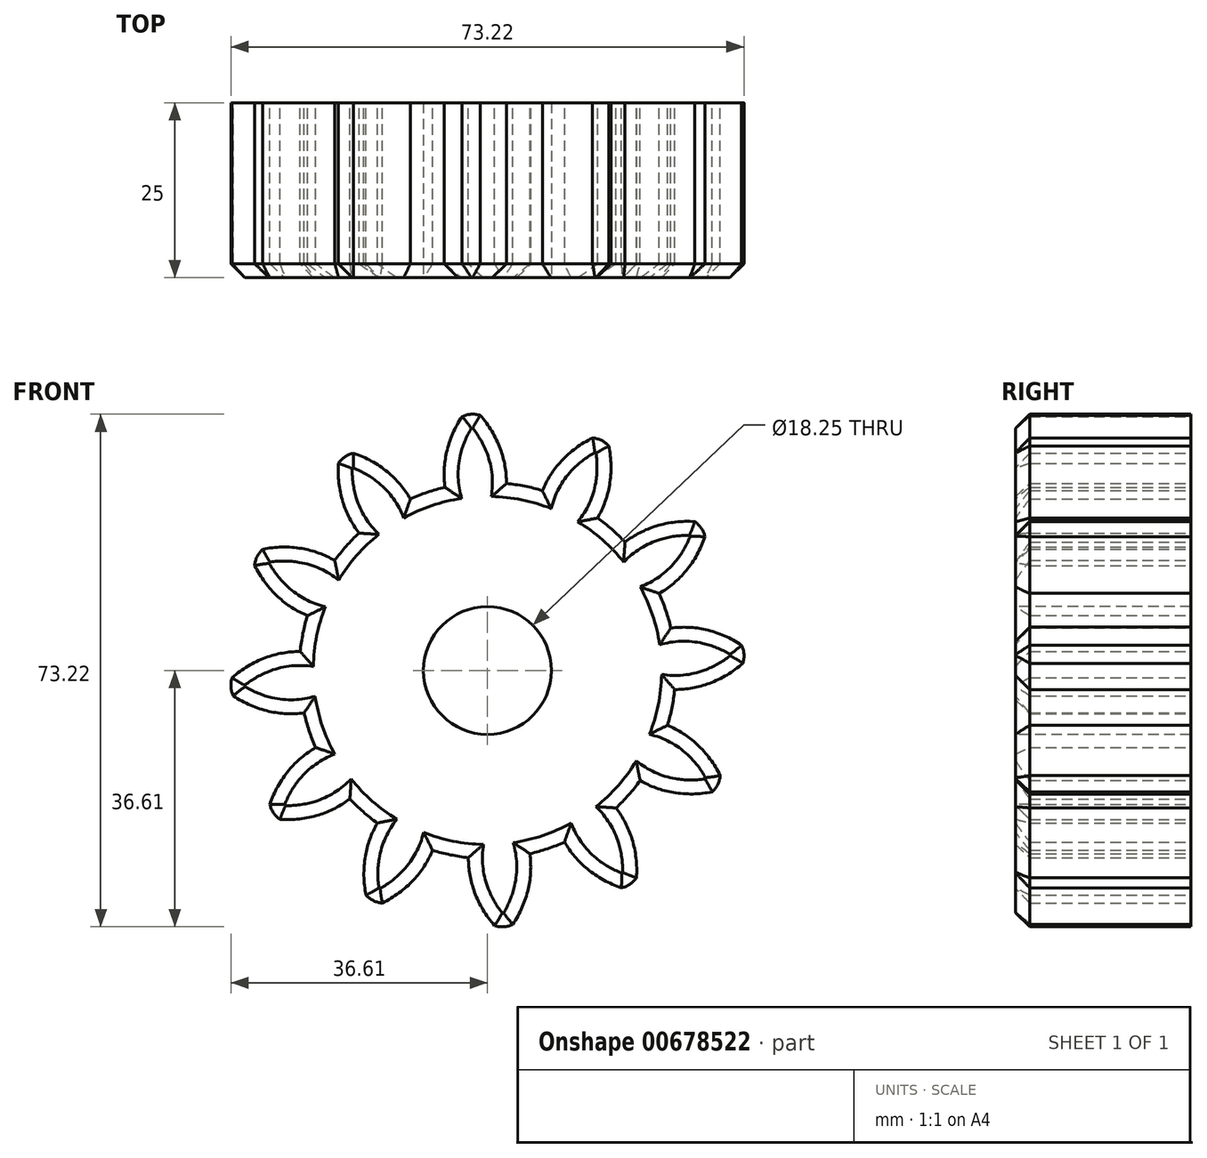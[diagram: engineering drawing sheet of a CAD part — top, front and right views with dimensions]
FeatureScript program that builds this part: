
annotation { "Feature Type Name" : "Feature", "Feature Type Description" : "" }
export const myFeature = defineFeature(function(context is Context, id is Id, definition is map)
    precondition{}
    {
        {
            var Q0;
            Q0=qCreatedBy(makeId("Front.planeOp"),FACE);
            var sketch = newSketch(context, id + "F0", { "sketchPlane" : qUnion([Q0])});
            skCircle(sketch, "E0", {"center": v(0, 0) * mm, "radius": 26.86 * mm});
            skCircle(sketch, "E1", {"center": v(0, 0) * mm, "radius": 29.34 * mm, "construction": true});
            skCircle(sketch, "E2", {"center": v(0, 0) * mm, "radius": 31.75 * mm, "construction": true});
            skLineSegment(sketch, "E3", {"start": v(0, 0) * mm, "end": v(0, 50.88) * mm, "construction": true});
            skLineSegment(sketch, "E4", {"start": v(0, 0) * mm, "end": v(-3.38, 51.5) * mm, "construction": true});
            skLineSegment(sketch, "E5", {"start": v(0, 29.36) * mm, "end": v(-19.52, 29.36) * mm, "construction": true});
            skLineSegment(sketch, "E6", {"start": v(0, 29.36) * mm, "end": v(-21.27, 21.62) * mm, "construction": true});
            skCircle(sketch, "E7", {"center": v(0, 0) * mm, "radius": 27.59 * mm, "construction": true});
            skArc(sketch, "E8", {"start": v(1.83, 31.67) * mm, "mid": v(0.62, 34.19) * mm, "end": v(-1.02, 36.44) * mm});
            skArc(sketch, "E9", {"start": v(2.71, 26.71) * mm, "mid": v(2.5, 29.23) * mm, "end": v(1.83, 31.67) * mm});
            skArc(sketch, "E10.MirrorCS", {"start": v(-5.83, 31.17) * mm, "mid": v(-4.96, 33.82) * mm, "end": v(-3.62, 36.27) * mm});
            skArc(sketch, "E11.MirrorCS", {"start": v(-6.05, 26.14) * mm, "mid": v(-6.17, 28.67) * mm, "end": v(-5.83, 31.17) * mm});
            skArc(sketch, "E12", {"start": v(-1.02, 36.44) * mm, "mid": v(-2.34, 36.6) * mm, "end": v(-3.62, 36.27) * mm});
            skSolve(sketch);
        }
        {
            var Q0;
            {var subQ0=sQuery(id+"F0.wireOp",EDGE,"E0");var subQ1=makeQuery(id+"F0.imprint","INTERSECT",VERTEX,{"derivedFrom":[subQ0,sQuery(id+"F0.wireOp",EDGE,"E9")]});Q0=makeQuery(id+"F0.imprint","IMPRINT",FACE,{"disambiguationData":[TD([[makeQuery(id+"F0.imprint","IMPRINT",EDGE,{"disambiguationData":[TD([[subQ1,-1.0]])],"derivedFrom":subQ0}),1.0]])]});}
            var Q1;
            {var subQ2=sQuery(id+"F0.wireOp",EDGE,"E8");Q1=makeQuery(id+"F0.imprint","IMPRINT",FACE,{"disambiguationData":[TD([[makeQuery(id+"F0.imprint","IMPRINT",EDGE,{"derivedFrom":subQ2}),1.0]])]});}
            extrude(context, id + "F1", {"entities" : qUnion([Q0, Q1]), "depth" : 25 * mm, "offsetDistance" : 25 * mm});
        }
        {
            var Q0;
            Q0=makeQuery(id+"F1.opExtrude","SWEPT_BODY",BODY,{"disambiguationData":[OSD([sQuery(id+"F0.wireOp",EDGE,"E0"),sQuery(id+"F0.wireOp",EDGE,"E8"),sQuery(id+"F0.wireOp",EDGE,"E9"),sQuery(id+"F0.wireOp",EDGE,"E10.MirrorCS"),sQuery(id+"F0.wireOp",EDGE,"E11.MirrorCS"),sQuery(id+"F0.wireOp",EDGE,"E12")])]});
            var Q1;
            Q1=makeQuery(id+"F1.opExtrude","SWEPT_FACE",FACE,{"disambiguationData":[OSD([sQuery(id+"F0.wireOp",EDGE,"E0")])]});
            circularPattern(context, id + "F2", {"operationType" : NewBodyOperationType.ADD, "entities" : qUnion([Q0]), "axis" : qUnion([Q1]), "angle" : 360 * degree, "instanceCount" : 12, "equalSpace" : true});
        }
        {
            var Q0;
            {var subQ0=makeQuery(id+"F1.opExtrude","CAP_FACE",FACE,{"disambiguationData":[OSD([sQuery(id+"F0.wireOp",EDGE,"E0"),sQuery(id+"F0.wireOp",EDGE,"E8"),sQuery(id+"F0.wireOp",EDGE,"E9"),sQuery(id+"F0.wireOp",EDGE,"E10.MirrorCS"),sQuery(id+"F0.wireOp",EDGE,"E11.MirrorCS"),sQuery(id+"F0.wireOp",EDGE,"E12")])],"isStart":false});Q0=makeQuery(id+"F2.boolean.opBoolean","MERGE",FACE,{"derivedFrom":[subQ0,makeQuery(id+"F2.opPattern","COPY",FACE,{"derivedFrom":subQ0,"instanceName":"1"}),makeQuery(id+"F2.opPattern","COPY",FACE,{"derivedFrom":subQ0,"instanceName":"2"}),makeQuery(id+"F2.opPattern","COPY",FACE,{"derivedFrom":subQ0,"instanceName":"3"}),makeQuery(id+"F2.opPattern","COPY",FACE,{"derivedFrom":subQ0,"instanceName":"4"}),makeQuery(id+"F2.opPattern","COPY",FACE,{"derivedFrom":subQ0,"instanceName":"5"}),makeQuery(id+"F2.opPattern","COPY",FACE,{"derivedFrom":subQ0,"instanceName":"6"}),makeQuery(id+"F2.opPattern","COPY",FACE,{"derivedFrom":subQ0,"instanceName":"7"}),makeQuery(id+"F2.opPattern","COPY",FACE,{"derivedFrom":subQ0,"instanceName":"8"}),makeQuery(id+"F2.opPattern","COPY",FACE,{"derivedFrom":subQ0,"instanceName":"9"}),makeQuery(id+"F2.opPattern","COPY",FACE,{"derivedFrom":subQ0,"instanceName":"10"}),makeQuery(id+"F2.opPattern","COPY",FACE,{"derivedFrom":subQ0,"instanceName":"11"})]});}
            chamfer(context, id + "F3", {"entities" : qUnion([Q0]), "width" : 2 * mm, "tangentPropagation" : true});
        }
        {
            var Q0;
            {var subQ0=makeQuery(id+"F1.opExtrude","CAP_FACE",FACE,{"disambiguationData":[OSD([sQuery(id+"F0.wireOp",EDGE,"E0"),sQuery(id+"F0.wireOp",EDGE,"E8"),sQuery(id+"F0.wireOp",EDGE,"E9"),sQuery(id+"F0.wireOp",EDGE,"E10.MirrorCS"),sQuery(id+"F0.wireOp",EDGE,"E11.MirrorCS"),sQuery(id+"F0.wireOp",EDGE,"E12")])],"isStart":false});Q0=makeQuery(id+"F2.boolean.opBoolean","MERGE",FACE,{"derivedFrom":[subQ0,makeQuery(id+"F2.opPattern","COPY",FACE,{"derivedFrom":subQ0,"instanceName":"1"}),makeQuery(id+"F2.opPattern","COPY",FACE,{"derivedFrom":subQ0,"instanceName":"2"}),makeQuery(id+"F2.opPattern","COPY",FACE,{"derivedFrom":subQ0,"instanceName":"3"}),makeQuery(id+"F2.opPattern","COPY",FACE,{"derivedFrom":subQ0,"instanceName":"4"}),makeQuery(id+"F2.opPattern","COPY",FACE,{"derivedFrom":subQ0,"instanceName":"5"}),makeQuery(id+"F2.opPattern","COPY",FACE,{"derivedFrom":subQ0,"instanceName":"6"}),makeQuery(id+"F2.opPattern","COPY",FACE,{"derivedFrom":subQ0,"instanceName":"7"}),makeQuery(id+"F2.opPattern","COPY",FACE,{"derivedFrom":subQ0,"instanceName":"8"}),makeQuery(id+"F2.opPattern","COPY",FACE,{"derivedFrom":subQ0,"instanceName":"9"}),makeQuery(id+"F2.opPattern","COPY",FACE,{"derivedFrom":subQ0,"instanceName":"10"}),makeQuery(id+"F2.opPattern","COPY",FACE,{"derivedFrom":subQ0,"instanceName":"11"})]});}
            var sketch = newSketch(context, id + "F4", { "sketchPlane" : qUnion([Q0])});
            skCircle(sketch, "E13", {"center": v(0, 0) * mm, "radius": 9.13 * mm});
            skSolve(sketch);
        }
        {
            var Q0;
            Q0=makeQuery(id+"F4.imprint","IMPRINT",FACE,{"disambiguationData":[TD([[makeQuery(id+"F4.imprint","IMPRINT",EDGE,{"derivedFrom":sQuery(id+"F4.wireOp",EDGE,"E13")}),1.0]])]});
            extrude(context, id + "F5", {"entities" : qUnion([Q0]), "operationType" : NewBodyOperationType.REMOVE, "oppositeDirection" : true, "depth" : 25 * mm, "offsetDistance" : 25 * mm});
        }
    });
